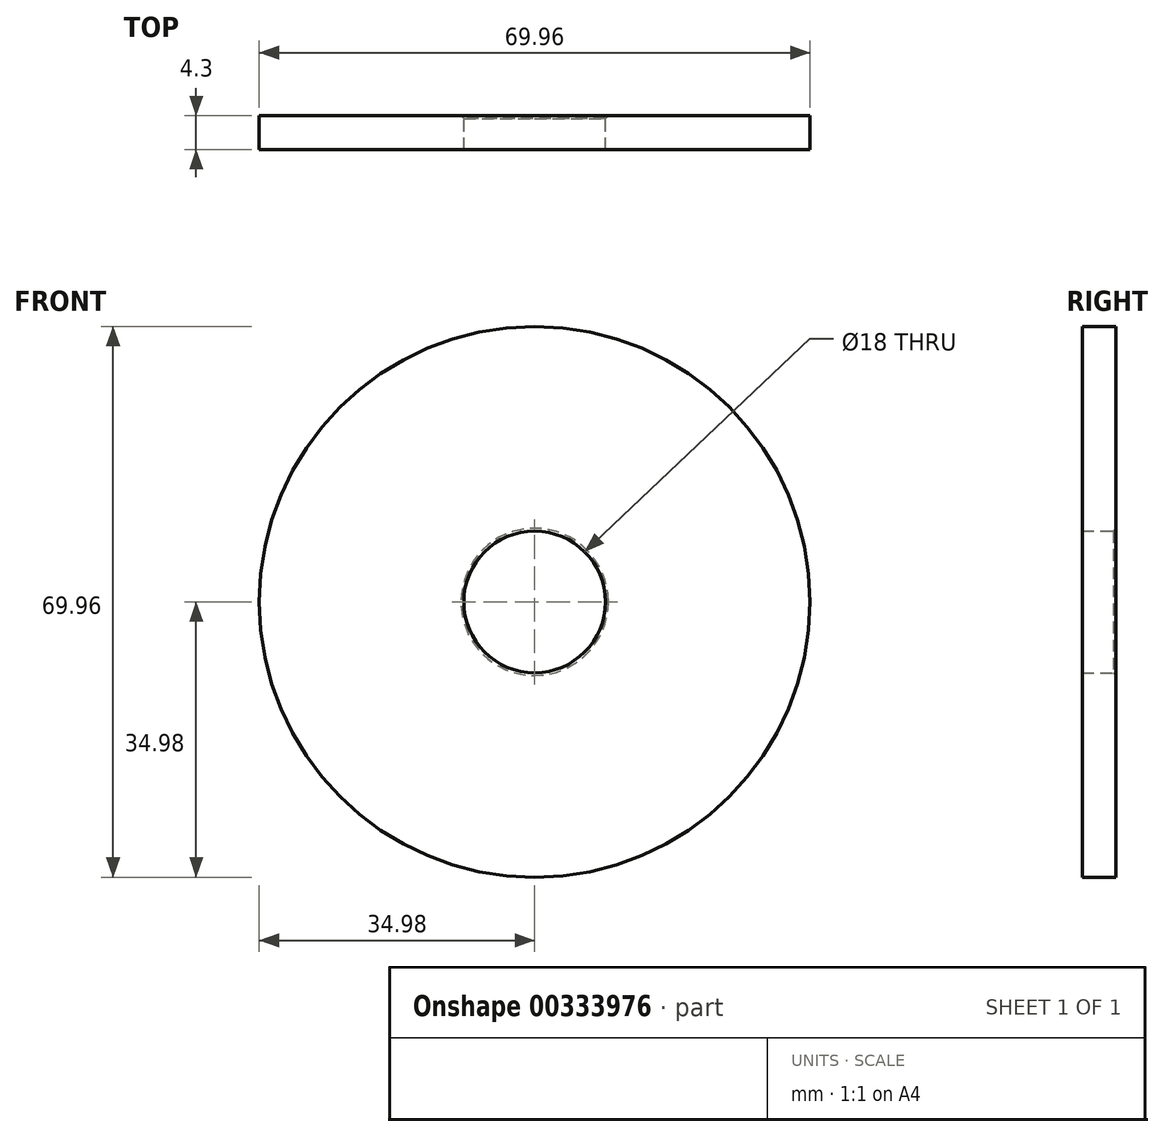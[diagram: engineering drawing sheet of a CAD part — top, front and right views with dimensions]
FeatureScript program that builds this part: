
annotation { "Feature Type Name" : "Feature", "Feature Type Description" : "" }
export const myFeature = defineFeature(function(context is Context, id is Id, definition is map)
    precondition{}
    {
        {
            var Q0;
            Q0=qCreatedBy(makeId("Front.planeOp"),FACE);
            var sketch = newSketch(context, id + "F0", { "sketchPlane" : qUnion([Q0])});
            skCircle(sketch, "E0", {"center": v(0, 0) * mm, "radius": 34.98 * mm});
            skSolve(sketch);
        }
        {
            var Q0;
            Q0 = qSketchRegion(id + "F0", true);
            extrude(context, id + "F1", {"entities" : qUnion([Q0]), "depth" : 4.3 * mm});
        }
        {
            var Q0;
            Q0=makeQuery(id+"F1.opExtrude","CAP_FACE",FACE,{"disambiguationData":[OSD([sQuery(id+"F0.wireOp",EDGE,"E0")])],"isStart":true});
            var sketch = newSketch(context, id + "F2", { "sketchPlane" : qUnion([Q0])});
            skCircle(sketch, "E1", {"center": v(0, 0) * mm, "radius": 3.86 * mm});
            skSolve(sketch);
        }
        {
            var Q0;
            Q0=sQuery(id+"F2.wireOp",VERTEX,"E1.center");
            var Q1;
            Q1=makeQuery(id+"F1.opExtrude","SWEPT_BODY",BODY,{"disambiguationData":[OSD([sQuery(id+"F0.wireOp",EDGE,"E0")])]});
            hole(context, id + "F3", {"style" : HoleStyle.C_SINK, "endStyle" : HoleEndStyle.THROUGH, "holeDiameter" : 18 * mm, "cSinkDiameter" : 18.7 * mm, "cSinkAngle" : 90 * degree, "majorDiameter" : 5 * mm, "tappedDepth" : 12 * mm, "tapClearance" : 3, "startFromSketch" : true, "locations" : qUnion([Q0]), "scope" : qUnion([Q1])});
        }
    });
